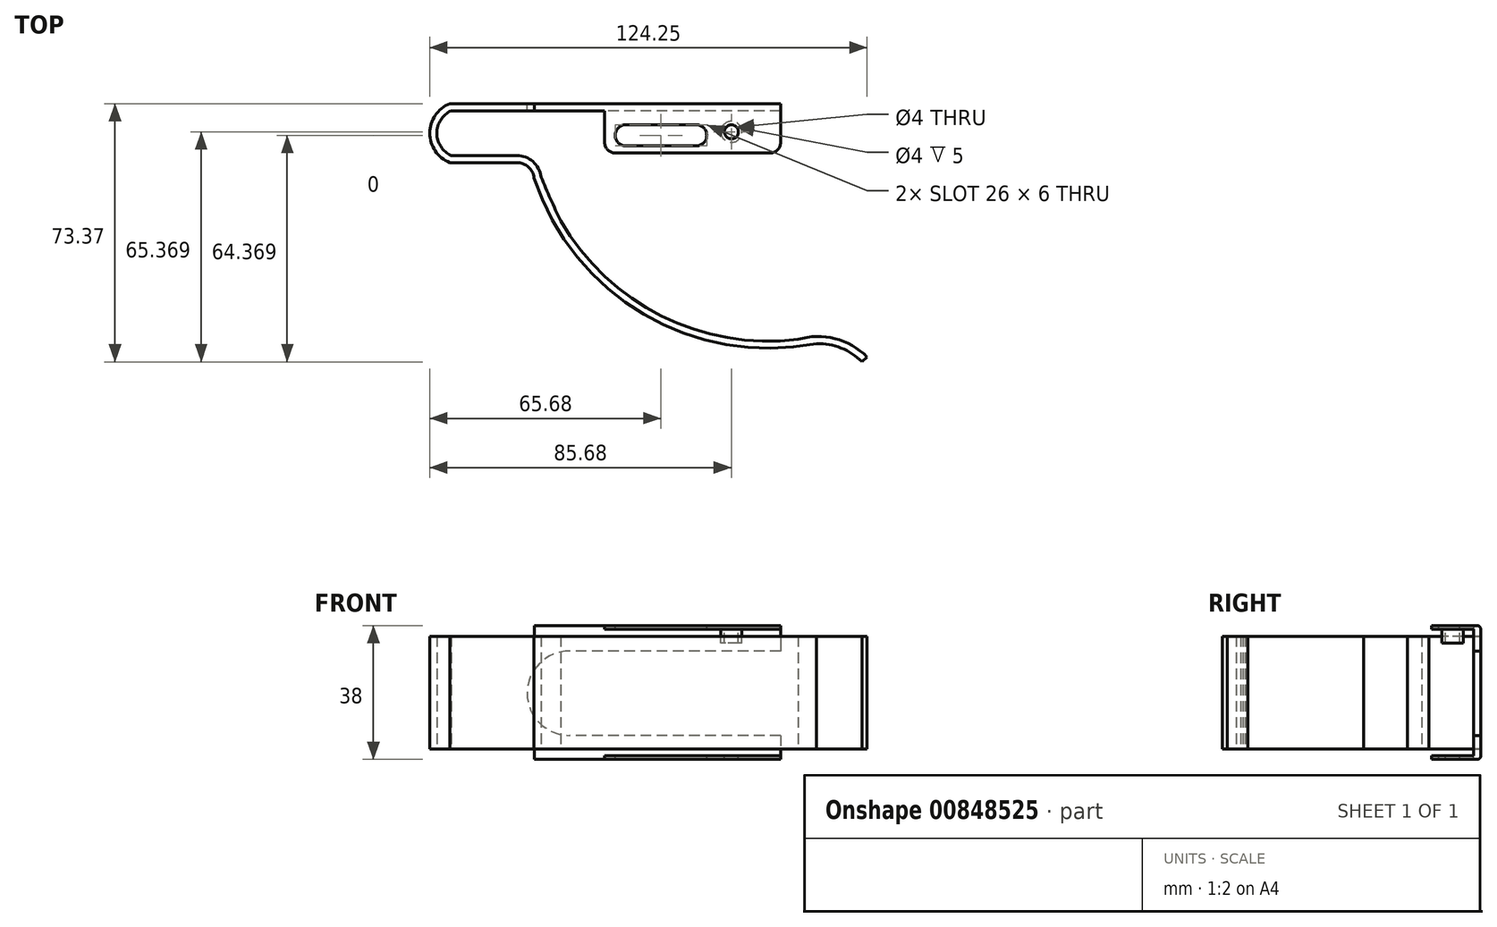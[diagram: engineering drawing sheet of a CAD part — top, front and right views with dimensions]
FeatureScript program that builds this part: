
annotation { "Feature Type Name" : "Feature", "Feature Type Description" : "" }
export const myFeature = defineFeature(function(context is Context, id is Id, definition is map)
    precondition{}
    {
        {
            var Q0;
            Q0=qCreatedBy(makeId("Top.planeOp"),FACE);
            var sketch = newSketch(context, id + "F0", { "sketchPlane" : qUnion([Q0])});
            skLineSegment(sketch, "E0", {"start": v(94, 40.3) * mm, "end": v(94, 38.3) * mm});
            skLineSegment(sketch, "E1", {"start": v(94, 38.3) * mm, "end": v(0, 38.3) * mm});
            skLineSegment(sketch, "E2", {"start": v(94, 40.3) * mm, "end": v(0, 40.3) * mm});
            skLineSegment(sketch, "E3", {"start": v(0, 23.57) * mm, "end": v(19, 23.57) * mm});
            skLineSegment(sketch, "E4", {"start": v(0, 25.57) * mm, "end": v(19, 25.57) * mm});
            skArc(sketch, "E5", {"start": v(0, 40.3) * mm, "mid": v(-5.68, 31.93) * mm, "end": v(0, 23.57) * mm});
            skArc(sketch, "E6", {"start": v(25.94, 19.5) * mm, "mid": v(23.6, 23.84) * mm, "end": v(19, 25.57) * mm});
            skArc(sketch, "E7", {"start": v(23.96, 19.23) * mm, "mid": v(22.3, 22.33) * mm, "end": v(19, 23.57) * mm});
            skArc(sketch, "E8", {"start": v(23.96, 19.23) * mm, "mid": v(55.09, -19.57) * mm, "end": v(104.13, -27.89) * mm});
            skArc(sketch, "E9.0", {"start": v(31.54, 7) * mm, "mid": v(60.14, -20.04) * mm, "end": v(98.92, -26.7) * mm});
            skArc(sketch, "E10.0", {"start": v(0.56, 38.37) * mm, "mid": v(-3.68, 31.83) * mm, "end": v(0.74, 25.43) * mm});
            skArc(sketch, "E11", {"start": v(118.57, -31.7) * mm, "mid": v(109.44, -26.47) * mm, "end": v(98.92, -26.7) * mm});
            skArc(sketch, "E12.0", {"start": v(117.1, -33.07) * mm, "mid": v(109.75, -28.63) * mm, "end": v(101.18, -28.2) * mm});
            skLineSegment(sketch, "E13", {"start": v(118.57, -31.7) * mm, "end": v(117.1, -33.07) * mm});
            skArc(sketch, "E14", {"start": v(25.94, 19.5) * mm, "mid": v(28.62, 13.2) * mm, "end": v(31.54, 7) * mm});
            skLineSegment(sketch, "E15", {"start": v(104.13, -27.89) * mm, "end": v(104.2, -27.86) * mm});
            skSolve(sketch);
        }
        {
            var Q0;
            {var subQ5=sQuery(id+"F0.wireOp",EDGE,"E0");Q0=makeQuery(id+"F0.imprint","IMPRINT",FACE,{"disambiguationData":[TD([[makeQuery(id+"F0.imprint","IMPRINT",EDGE,{"derivedFrom":subQ5}),-1.0]])]});}
            extrude(context, id + "F1", {"entities" : qUnion([Q0]), "depth" : 16 * mm, "offsetDistance" : 25 * mm});
        }
        {
            var Q0;
            Q0=makeQuery(id+"F1.opExtrude","SWEPT_FACE",FACE,{"disambiguationData":[OSD([sQuery(id+"F0.wireOp",EDGE,"E2")])]});
            var sketch = newSketch(context, id + "F2", { "sketchPlane" : qUnion([Q0])});
            skLineSegment(sketch, "E16.bottom", {"start": v(-94, 16) * mm, "end": v(-24, 16) * mm});
            skLineSegment(sketch, "E16.top", {"start": v(-94, 19) * mm, "end": v(-24, 19) * mm});
            skLineSegment(sketch, "E16.left", {"start": v(-94, 16) * mm, "end": v(-94, 19) * mm});
            skLineSegment(sketch, "E16.right", {"start": v(-24, 16) * mm, "end": v(-24, 19) * mm});
            skSolve(sketch);
        }
        {
            var Q0;
            Q0 = qSketchRegion(id + "F2", true);
            extrude(context, id + "F3", {"entities" : qUnion([Q0]), "operationType" : NewBodyOperationType.ADD, "oppositeDirection" : true, "depth" : 2 * mm, "offsetDistance" : 25 * mm});
        }
        {
            var Q0;
            Q0=makeQuery(id+"F3.opExtrude","SWEPT_FACE",FACE,{"disambiguationData":[OSD([sQuery(id+"F2.wireOp",EDGE,"E16.top")])]});
            var sketch = newSketch(context, id + "F4", { "sketchPlane" : qUnion([Q0])});
            skLineSegment(sketch, "E17.bottom", {"start": v(94, 40.3) * mm, "end": v(44, 40.3) * mm});
            skLineSegment(sketch, "E17.top", {"start": v(94, 26.3) * mm, "end": v(44, 26.3) * mm});
            skLineSegment(sketch, "E17.left", {"start": v(94, 40.3) * mm, "end": v(94, 26.3) * mm});
            skLineSegment(sketch, "E17.right", {"start": v(44, 40.3) * mm, "end": v(44, 26.3) * mm});
            skSolve(sketch);
        }
        {
            var Q0;
            {var subQ0=sQuery(id+"F4.wireOp",EDGE,"E17.bottom");Q0=makeQuery(id+"F4.imprint","IMPRINT",FACE,{"disambiguationData":[TD([[makeQuery(id+"F4.imprint","IMPRINT",EDGE,{"derivedFrom":subQ0}),1.0]])]});}
            var Q1;
            {var subQ0=sQuery(id+"F4.wireOp",EDGE,"E17.top");Q1=makeQuery(id+"F4.imprint","IMPRINT",FACE,{"disambiguationData":[TD([[makeQuery(id+"F4.imprint","IMPRINT",EDGE,{"derivedFrom":subQ0}),-1.0]])]});}
            extrude(context, id + "F5", {"entities" : qUnion([Q0, Q1]), "operationType" : NewBodyOperationType.ADD, "oppositeDirection" : true, "depth" : 1 * mm, "offsetDistance" : 25 * mm});
        }
        {
            var Q0;
            Q0=makeQuery(id+"F3.opExtrude","CAP_EDGE",EDGE,{"disambiguationData":[OSD([sQuery(id+"F2.wireOp",EDGE,"E16.top")])],"isStart":true});
            fillet(context, id + "F6", {"entities" : qUnion([Q0]), "radius" : 1 * mm, "tangentPropagation" : true, "allowEdgeOverflow" : false});
        }
        {
            var Q0;
            Q0=makeQuery(id+"F1.opExtrude","SWEPT_BODY",BODY,{"disambiguationData":[OSD([sQuery(id+"F0.wireOp",EDGE,"E0"),sQuery(id+"F0.wireOp",EDGE,"E1"),sQuery(id+"F0.wireOp",EDGE,"E2"),sQuery(id+"F0.wireOp",EDGE,"E3"),sQuery(id+"F0.wireOp",EDGE,"E4"),sQuery(id+"F0.wireOp",EDGE,"E5"),sQuery(id+"F0.wireOp",EDGE,"E6"),sQuery(id+"F0.wireOp",EDGE,"E7"),sQuery(id+"F0.wireOp",EDGE,"E8"),sQuery(id+"F0.wireOp",EDGE,"E9.0"),sQuery(id+"F0.wireOp",EDGE,"E10.0"),sQuery(id+"F0.wireOp",EDGE,"E11"),sQuery(id+"F0.wireOp",EDGE,"E12.0"),sQuery(id+"F0.wireOp",EDGE,"E13"),sQuery(id+"F0.wireOp",EDGE,"E14"),sQuery(id+"F0.wireOp",EDGE,"E15")])]});
            var Q1;
            Q1=makeQuery(id+"F1.opExtrude","CAP_FACE",FACE,{"disambiguationData":[OSD([sQuery(id+"F0.wireOp",EDGE,"E0"),sQuery(id+"F0.wireOp",EDGE,"E1"),sQuery(id+"F0.wireOp",EDGE,"E2"),sQuery(id+"F0.wireOp",EDGE,"E3"),sQuery(id+"F0.wireOp",EDGE,"E4"),sQuery(id+"F0.wireOp",EDGE,"E5"),sQuery(id+"F0.wireOp",EDGE,"E6"),sQuery(id+"F0.wireOp",EDGE,"E7"),sQuery(id+"F0.wireOp",EDGE,"E8"),sQuery(id+"F0.wireOp",EDGE,"E9.0"),sQuery(id+"F0.wireOp",EDGE,"E10.0"),sQuery(id+"F0.wireOp",EDGE,"E11"),sQuery(id+"F0.wireOp",EDGE,"E12.0"),sQuery(id+"F0.wireOp",EDGE,"E13"),sQuery(id+"F0.wireOp",EDGE,"E14"),sQuery(id+"F0.wireOp",EDGE,"E15")])],"isStart":true});
            mirror(context, id + "F7", {"operationType" : NewBodyOperationType.ADD, "entities" : qUnion([Q0]), "mirrorPlane" : qUnion([Q1])});
        }
        {
            var Q0;
            {var subQ0=makeQuery(id+"F3.boolean.opBoolean","MERGE",FACE,{"derivedFrom":[makeQuery(id+"F1.opExtrude","SWEPT_FACE",FACE,{"disambiguationData":[OSD([sQuery(id+"F0.wireOp",EDGE,"E2")])]}),makeQuery(id+"F3.opExtrude","CAP_FACE",FACE,{"disambiguationData":[OSD([sQuery(id+"F2.wireOp",EDGE,"E16.bottom"),sQuery(id+"F2.wireOp",EDGE,"E16.top"),sQuery(id+"F2.wireOp",EDGE,"E16.left"),sQuery(id+"F2.wireOp",EDGE,"E16.right")])],"isStart":true})]});Q0=makeQuery(id+"F7.boolean.opBoolean","MERGE",FACE,{"derivedFrom":[subQ0,makeQuery(id+"F7.opPattern","COPY",FACE,{"derivedFrom":subQ0,"instanceName":"1"})]});}
            var sketch = newSketch(context, id + "F8", { "sketchPlane" : qUnion([Q0])});
            skLineSegment(sketch, "E18", {"start": v(-94, 11.81) * mm, "end": v(-34, 11.81) * mm});
            skLineSegment(sketch, "E19", {"start": v(-94, -12.19) * mm, "end": v(-34, -12.19) * mm});
            skArc(sketch, "E20", {"start": v(-34, -12.19) * mm, "mid": v(-22, -0.19) * mm, "end": v(-34, 11.81) * mm});
            skSolve(sketch);
        }
        {
            var Q0;
            {var subQ0=sQuery(id+"F8.wireOp",EDGE,"E18");Q0=makeQuery(id+"F8.imprint","IMPRINT",FACE,{"disambiguationData":[TD([[makeQuery(id+"F8.imprint","IMPRINT",EDGE,{"derivedFrom":subQ0}),-1.0]])]});}
            extrude(context, id + "F9", {"entities" : qUnion([Q0]), "operationType" : NewBodyOperationType.REMOVE, "oppositeDirection" : true, "depth" : 2 * mm, "offsetDistance" : 25 * mm});
        }
        {
            var Q0;
            Q0=makeQuery(id+"F5.boolean.opBoolean","MERGE",FACE,{"derivedFrom":[makeQuery(id+"F3.opExtrude","SWEPT_FACE",FACE,{"disambiguationData":[OSD([sQuery(id+"F2.wireOp",EDGE,"E16.top")])]}),makeQuery(id+"F5.opExtrude","CAP_FACE",FACE,{"disambiguationData":[OSD([sQuery(id+"F4.wireOp",EDGE,"E17.bottom"),sQuery(id+"F4.wireOp",EDGE,"E17.top"),sQuery(id+"F4.wireOp",EDGE,"E17.left"),sQuery(id+"F4.wireOp",EDGE,"E17.right")])],"isStart":true})]});
            var sketch = newSketch(context, id + "F10", { "sketchPlane" : qUnion([Q0])});
            skLineSegment(sketch, "E21", {"start": v(50, 31.3) * mm, "end": v(70, 31.3) * mm});
            skArc(sketch, "E22.0.startCap", {"start": v(50, 28.3) * mm, "mid": v(47, 31.3) * mm, "end": v(50, 34.3) * mm});
            skArc(sketch, "E22.0.endCap", {"start": v(70, 34.3) * mm, "mid": v(73, 31.3) * mm, "end": v(70, 28.3) * mm});
            skLineSegment(sketch, "E22.0.left", {"start": v(50, 34.3) * mm, "end": v(70, 34.3) * mm});
            skLineSegment(sketch, "E22.0.right", {"start": v(50, 28.3) * mm, "end": v(70, 28.3) * mm});
            skSolve(sketch);
        }
        {
            var Q0;
            Q0 = qSketchRegion(id + "F10", true);
            extrude(context, id + "F11", {"entities" : qUnion([Q0]), "operationType" : NewBodyOperationType.REMOVE, "endBound" : BoundingType.THROUGH_ALL, "oppositeDirection" : true, "depth" : 25 * mm, "offsetDistance" : 25 * mm});
        }
        {
            var Q0;
            Q0=makeQuery(id+"F5.boolean.opBoolean","MERGE",FACE,{"derivedFrom":[makeQuery(id+"F3.opExtrude","SWEPT_FACE",FACE,{"disambiguationData":[OSD([sQuery(id+"F2.wireOp",EDGE,"E16.top")])]}),makeQuery(id+"F5.opExtrude","CAP_FACE",FACE,{"disambiguationData":[OSD([sQuery(id+"F4.wireOp",EDGE,"E17.bottom"),sQuery(id+"F4.wireOp",EDGE,"E17.top"),sQuery(id+"F4.wireOp",EDGE,"E17.left"),sQuery(id+"F4.wireOp",EDGE,"E17.right")])],"isStart":true})]});
            var sketch = newSketch(context, id + "F12", { "sketchPlane" : qUnion([Q0])});
            skPoint(sketch, "E23", {"position": v(80, 32.3) * mm});
            skSolve(sketch);
        }
        {
            var Q0;
            Q0=sQuery(id+"F12.wireOp",VERTEX,"E23");
            var Q1;
            Q1=makeQuery(id+"F1.opExtrude","SWEPT_BODY",BODY,{"disambiguationData":[OSD([sQuery(id+"F0.wireOp",EDGE,"E0"),sQuery(id+"F0.wireOp",EDGE,"E1"),sQuery(id+"F0.wireOp",EDGE,"E2"),sQuery(id+"F0.wireOp",EDGE,"E3"),sQuery(id+"F0.wireOp",EDGE,"E4"),sQuery(id+"F0.wireOp",EDGE,"E5"),sQuery(id+"F0.wireOp",EDGE,"E6"),sQuery(id+"F0.wireOp",EDGE,"E7"),sQuery(id+"F0.wireOp",EDGE,"E8"),sQuery(id+"F0.wireOp",EDGE,"E9.0"),sQuery(id+"F0.wireOp",EDGE,"E10.0"),sQuery(id+"F0.wireOp",EDGE,"E11"),sQuery(id+"F0.wireOp",EDGE,"E12.0"),sQuery(id+"F0.wireOp",EDGE,"E13"),sQuery(id+"F0.wireOp",EDGE,"E14"),sQuery(id+"F0.wireOp",EDGE,"E15")])]});
            hole(context, id + "F13", {"style" : HoleStyle.SIMPLE, "endStyle" : HoleEndStyle.BLIND, "holeDiameter" : 4 * mm, "majorDiameter" : 5 * mm, "holeDepth" : 50 * mm, "isTappedThrough" : true, "tappedDepth" : 12 * mm, "tapClearance" : 3, "locations" : qUnion([Q0]), "scope" : qUnion([Q1])});
        }
        {
            var Q0;
            Q0=makeQuery(id+"F5.boolean.opBoolean","MERGE",FACE,{"derivedFrom":[makeQuery(id+"F3.opExtrude","SWEPT_FACE",FACE,{"disambiguationData":[OSD([sQuery(id+"F2.wireOp",EDGE,"E16.top")])]}),makeQuery(id+"F5.opExtrude","CAP_FACE",FACE,{"disambiguationData":[OSD([sQuery(id+"F4.wireOp",EDGE,"E17.bottom"),sQuery(id+"F4.wireOp",EDGE,"E17.top"),sQuery(id+"F4.wireOp",EDGE,"E17.left"),sQuery(id+"F4.wireOp",EDGE,"E17.right")])],"isStart":true})]});
            var sketch = newSketch(context, id + "F14", { "sketchPlane" : qUnion([Q0])});
            skCircle(sketch, "E24", {"center": v(80, 32.3) * mm, "radius": 3 * mm});
            skSolve(sketch);
        }
        {
            var Q0;
            Q0=makeQuery(id+"F14.imprint","IMPRINT",FACE,{"disambiguationData":[TD([[makeQuery(id+"F14.imprint","IMPRINT",EDGE,{"derivedFrom":sQuery(id+"F14.wireOp",EDGE,"E24")}),1.0]])]});
            extrude(context, id + "F15", {"entities" : qUnion([Q0]), "operationType" : NewBodyOperationType.ADD, "oppositeDirection" : true, "depth" : 5 * mm, "offsetDistance" : 25 * mm});
        }
        {
            var Q0;
            Q0=makeQuery(id+"F5.opExtrude","SWEPT_EDGE",EDGE,{"disambiguationData":[OSD([sQuery(id+"F4.wireOp",EDGE,"E17.top"),sQuery(id+"F4.wireOp",EDGE,"E17.right")])]});
            var Q1;
            Q1=makeQuery(id+"F7.opPattern","COPY",EDGE,{"derivedFrom":makeQuery(id+"F5.opExtrude","SWEPT_EDGE",EDGE,{"disambiguationData":[OSD([sQuery(id+"F4.wireOp",EDGE,"E17.top"),sQuery(id+"F4.wireOp",EDGE,"E17.right")])]}),"instanceName":"1"});
            var Q2;
            Q2=makeQuery(id+"F7.opPattern","COPY",EDGE,{"derivedFrom":makeQuery(id+"F5.opExtrude","SWEPT_EDGE",EDGE,{"disambiguationData":[OSD([sQuery(id+"F4.wireOp",EDGE,"E17.top"),sQuery(id+"F4.wireOp",EDGE,"E17.left")])]}),"instanceName":"1"});
            var Q3;
            Q3=makeQuery(id+"F5.opExtrude","SWEPT_EDGE",EDGE,{"disambiguationData":[OSD([sQuery(id+"F4.wireOp",EDGE,"E17.top"),sQuery(id+"F4.wireOp",EDGE,"E17.left")])]});
            fillet(context, id + "F16", {"entities" : qUnion([Q0, Q1, Q2, Q3]), "radius" : 3 * mm, "tangentPropagation" : true, "allowEdgeOverflow" : false});
        }
    });
